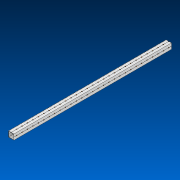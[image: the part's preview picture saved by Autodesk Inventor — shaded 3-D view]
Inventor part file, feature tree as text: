
AUTODESK INVENTOR PART (.ipt)
format: ipt  version: 2022.2 (Build 262287000, 287)  size: 869,376 bytes
history: native  units: in
note: dims shown in document units (in); Inventor stores cm internally (conversion verified against a paired STEP export)
features: other x58, pattern_linear x2, extrude x1, sketch x1
ambient origin geometry x8: Origin, YZ Plane, XZ Plane, XY Plane, X Axis, Y Axis, Z Axis, Center Point
bodies: Solid1 (feature_tree)
feature tree (62):
  extrude  "Extrusion1"  TaperAngle=0.0deg  [1 undecoded]
  other  "Work Axis1"
  other  "Work Axis2"
  pattern_linear  "Rectangular Pattern1"  Count1=29  [1 undecoded]
  pattern_linear  "Rectangular Pattern2"  Spacing1=1.0in  [1 undecoded]
  sketch  "Sketch1"  dims[d0=30.0in d1=0.0in d2=11.4173in d4=1.0in d5=11.0236in d7=1.0in]
  other  "Work Axis3"
  other  "Work Axis4"
  other  "Work Axis5"
  other  "Work Axis6"
  other  "Work Axis7"
  other  "Work Axis8"
  other  "Work Axis9"
  other  "Work Axis10"
  other  "Work Axis11"
  other  "Work Axis12"
  other  "Work Axis13"
  other  "Work Axis14"
  other  "Work Axis15"
  other  "Work Axis16"
  other  "Work Axis17"
  other  "Work Axis18"
  other  "Work Axis19"
  other  "Work Axis20"
  other  "Work Axis21"
  other  "Work Axis22"
  other  "Work Axis23"
  other  "Work Axis24"
  other  "Work Axis25"
  other  "Work Axis26"
  other  "Work Axis27"
  other  "Work Axis28"
  other  "Work Axis29"
  other  "Work Axis30"
  other  "Work Axis31"
  other  "Work Axis32"
  other  "Work Axis63"
  other  "Work Axis64"
  other  "Work Axis65"
  other  "Work Axis66"
  other  "Work Axis67"
  other  "Work Axis68"
  other  "Work Axis69"
  other  "Work Axis70"
  other  "Work Axis71"
  other  "Work Axis72"
  other  "Work Axis73"
  other  "Work Axis74"
  other  "Work Axis75"
  other  "Work Axis76"
  other  "Work Axis77"
  other  "Work Axis78"
  other  "Work Axis79"
  other  "Work Axis80"
  other  "Work Axis81"
  other  "Work Axis82"
  other  "Work Axis83"
  other  "Work Axis84"
  other  "Work Axis85"
  other  "Work Axis86"
  other  "Work Axis87"
  other  "LPattern2"
note: 3 required parameter values undecoded (feature->parameter linkage not recoverable at this tier; creation-order binding heuristic only, values carry confidence <= 0.55)
